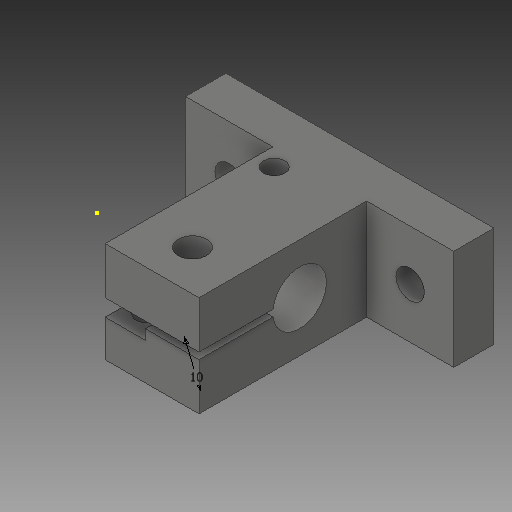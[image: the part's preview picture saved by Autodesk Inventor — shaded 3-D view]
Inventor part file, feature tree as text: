
AUTODESK INVENTOR PART (.ipt)
format: ipt  version: 2019 (Build 230136000, 136)  size: 348,160 bytes
history: native  units: in
note: dims shown in document units (in); Inventor stores cm internally (conversion verified against a paired STEP export)
features: sketch x9, extrude x8, other x3, reference x2
ambient origin geometry x8: Origin, YZ Plane, XZ Plane, XY Plane, X Axis, Y Axis, Z Axis, Center Point
bodies: Solid1 (feature_tree)
feature tree (22):
  extrude  "Extrusion1"  Depth=0.5906in
  extrude  "Extrusion2"  Depth=0.5512in
  extrude  "Extrusion4"  Depth=0.9843in
  extrude  "Extrusion5"  Depth=1.1811in TaperAngle=0.0deg
  extrude  "Extrusion6"  Depth=0.315in
  sketch  "Sketch7"  dims[d18=0.0394in d19=1.1811in d20=0.0in]
  sketch  "Sketch8"  dims[d21=0.1673in d22=0.2362in]
  extrude  "Extrusion8"  Depth=0.0394in TaperAngle=0.0deg
  extrude  "Extrusion9"  Depth=0.2362in
  sketch  "Sketch9"  dims[d23=1.1811in d24=0.0in d25=0.3937in]
  extrude  "Extrusion10"  Depth=0.3937in
  sketch  "Sketch1"  dims[d0=1.5748in d1=0.5906in]
  sketch  "Sketch2"  dims[d2=0.2362in d3=0.0in d4=0.5512in]
  sketch  "Sketch4"  dims[d5=0.9843in d6=0.0in d12=0.1673in]
  sketch  "Sketch5"  dims[d13=0.1673in d14=1.1811in d15=0.0in]
  sketch  "Sketch6"  dims[d16=0.315in d17=0.6299in]
  reference  "Reference1"
  reference  "Reference2"
  sketch  "Sketch10"  dims[d28=0.3937in d29=0.0in d30=0.3937in d31=0.0in d32=0.2362in d33=0.0591in d34=0.0in d35=0.2362in]
  other  "<userpath>\Stuff\Ajedrez2\Ajedrez2.iam"
  other  "Ajedrez2.iam"
  other  "Endstop mecânico - Chave fim de curso:2"
